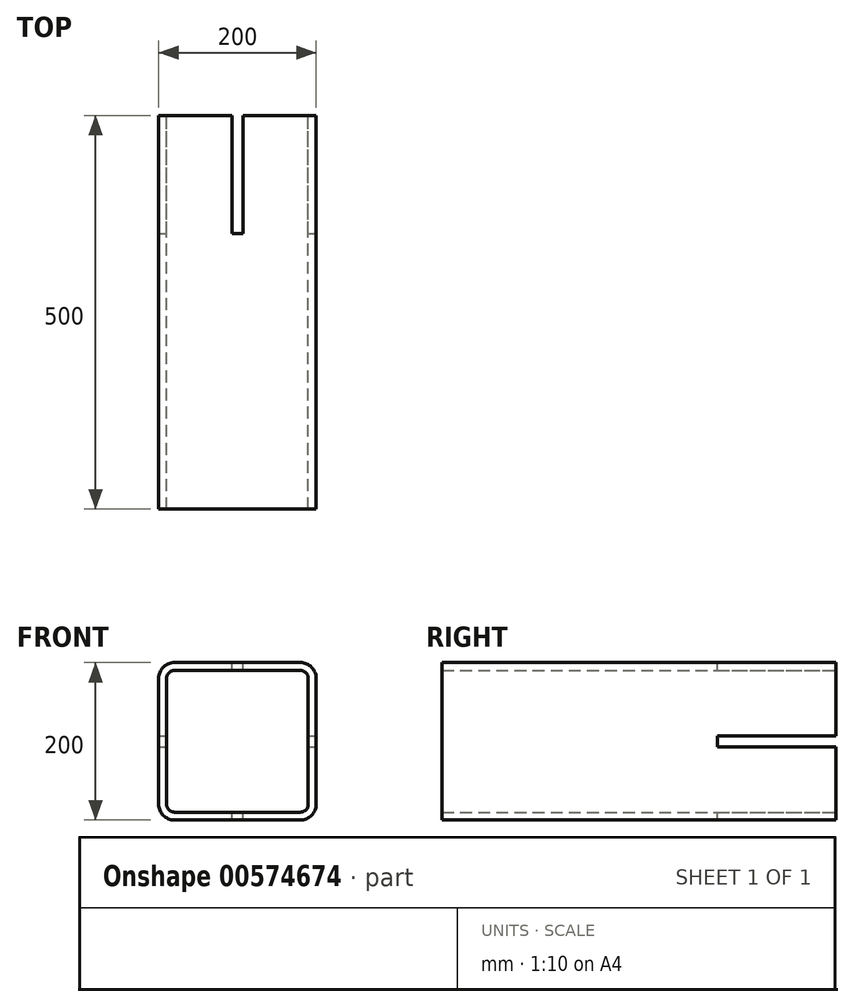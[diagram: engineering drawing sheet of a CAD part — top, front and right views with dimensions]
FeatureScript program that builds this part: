
annotation { "Feature Type Name" : "Feature", "Feature Type Description" : "" }
export const myFeature = defineFeature(function(context is Context, id is Id, definition is map)
    precondition{}
    {
        {
            var Q0;
            Q0=qCreatedBy(makeId("Front.planeOp"),FACE);
            var sketch = newSketch(context, id + "F0", { "sketchPlane" : qUnion([Q0])});
            skLineSegment(sketch, "E0.bottom", {"start": v(80, 100) * mm, "end": v(-80, 100) * mm});
            skLineSegment(sketch, "E0.top", {"start": v(80, -100) * mm, "end": v(-80, -100) * mm});
            skLineSegment(sketch, "E0.left", {"start": v(100, 80) * mm, "end": v(100, -80) * mm});
            skLineSegment(sketch, "E0.right", {"start": v(-100, 80) * mm, "end": v(-100, -80) * mm});
            skPoint(sketch, "E0.middle", {"position": v(0, 0) * mm});
            skLineSegment(sketch, "E1.0", {"start": v(80, 90) * mm, "end": v(-80, 90) * mm});
            skLineSegment(sketch, "E1.1", {"start": v(90, 80) * mm, "end": v(90, -80) * mm});
            skLineSegment(sketch, "E1.2", {"start": v(80, -90) * mm, "end": v(-80, -90) * mm});
            skLineSegment(sketch, "E1.3", {"start": v(-90, 80) * mm, "end": v(-90, -80) * mm});
            skPoint(sketch, "E2.visualSharp", {"position": v(90, 90) * mm});
            skArc(sketch, "E2.filletArc", {"start": v(90, 80) * mm, "mid": v(87.07, 87.07) * mm, "end": v(80, 90) * mm});
            skPoint(sketch, "E3.visualSharp", {"position": v(90, -90) * mm});
            skArc(sketch, "E3.filletArc", {"start": v(80, -90) * mm, "mid": v(87.07, -87.07) * mm, "end": v(90, -80) * mm});
            skPoint(sketch, "E4.visualSharp", {"position": v(-90, -90) * mm});
            skArc(sketch, "E4.filletArc", {"start": v(-90, -80) * mm, "mid": v(-87.07, -87.07) * mm, "end": v(-80, -90) * mm});
            skPoint(sketch, "E5.visualSharp", {"position": v(-90, 90) * mm});
            skArc(sketch, "E5.filletArc", {"start": v(-80, 90) * mm, "mid": v(-87.07, 87.07) * mm, "end": v(-90, 80) * mm});
            skPoint(sketch, "E6.visualSharp", {"position": v(100, 100) * mm});
            skArc(sketch, "E6.filletArc", {"start": v(100, 80) * mm, "mid": v(94.14, 94.14) * mm, "end": v(80, 100) * mm});
            skPoint(sketch, "E7.visualSharp", {"position": v(-100, 100) * mm});
            skArc(sketch, "E7.filletArc", {"start": v(-80, 100) * mm, "mid": v(-94.14, 94.14) * mm, "end": v(-100, 80) * mm});
            skPoint(sketch, "E8.visualSharp", {"position": v(-100, -100) * mm});
            skArc(sketch, "E8.filletArc", {"start": v(-100, -80) * mm, "mid": v(-94.14, -94.14) * mm, "end": v(-80, -100) * mm});
            skPoint(sketch, "E9.visualSharp", {"position": v(100, -100) * mm});
            skArc(sketch, "E9.filletArc", {"start": v(80, -100) * mm, "mid": v(94.14, -94.14) * mm, "end": v(100, -80) * mm});
            skSolve(sketch);
        }
        {
            var Q0;
            Q0=qSketchRegion(id+"F0",true);
            extrude(context, id + "F1", {"entities" : qUnion([Q0]), "depth" : 500 * mm, "offsetDistance" : 25 * mm});
        }
        {
            var Q0;
            Q0=makeQuery(id+"F1.opExtrude","SWEPT_FACE",FACE,{"disambiguationData":[OSD([sQuery(id+"F0.wireOp",EDGE,"E0.bottom")])]});
            var sketch = newSketch(context, id + "F2", { "sketchPlane" : qUnion([Q0])});
            skLineSegment(sketch, "E10.bottom", {"start": v(-7, 0) * mm, "end": v(7, 0) * mm});
            skLineSegment(sketch, "E10.top", {"start": v(-7, -150) * mm, "end": v(7, -150) * mm});
            skLineSegment(sketch, "E10.left", {"start": v(-7, 0) * mm, "end": v(-7, -150) * mm});
            skLineSegment(sketch, "E10.right", {"start": v(7, 0) * mm, "end": v(7, -150) * mm});
            skSolve(sketch);
        }
        {
            var Q0;
            Q0 = qSketchRegion(id + "F2", true);
            extrude(context, id + "F3", {"entities" : qUnion([Q0]), "operationType" : NewBodyOperationType.REMOVE, "endBound" : BoundingType.THROUGH_ALL, "oppositeDirection" : true, "depth" : 25 * mm, "offsetDistance" : 25 * mm});
        }
        {
            var Q0;
            Q0=makeQuery(id+"F1.opExtrude","SWEPT_FACE",FACE,{"disambiguationData":[OSD([sQuery(id+"F0.wireOp",EDGE,"E0.left")])]});
            var sketch = newSketch(context, id + "F4", { "sketchPlane" : qUnion([Q0])});
            skLineSegment(sketch, "E11.bottom", {"start": v(-150, 7) * mm, "end": v(0, 7) * mm});
            skLineSegment(sketch, "E11.top", {"start": v(-150, -7) * mm, "end": v(0, -7) * mm});
            skLineSegment(sketch, "E11.left", {"start": v(-150, 7) * mm, "end": v(-150, -7) * mm});
            skLineSegment(sketch, "E11.right", {"start": v(0, 7) * mm, "end": v(0, -7) * mm});
            skSolve(sketch);
        }
        {
            var Q0;
            Q0 = qSketchRegion(id + "F4", true);
            extrude(context, id + "F5", {"entities" : qUnion([Q0]), "operationType" : NewBodyOperationType.REMOVE, "endBound" : BoundingType.THROUGH_ALL, "oppositeDirection" : true, "depth" : 25 * mm, "offsetDistance" : 25 * mm});
        }
    });
